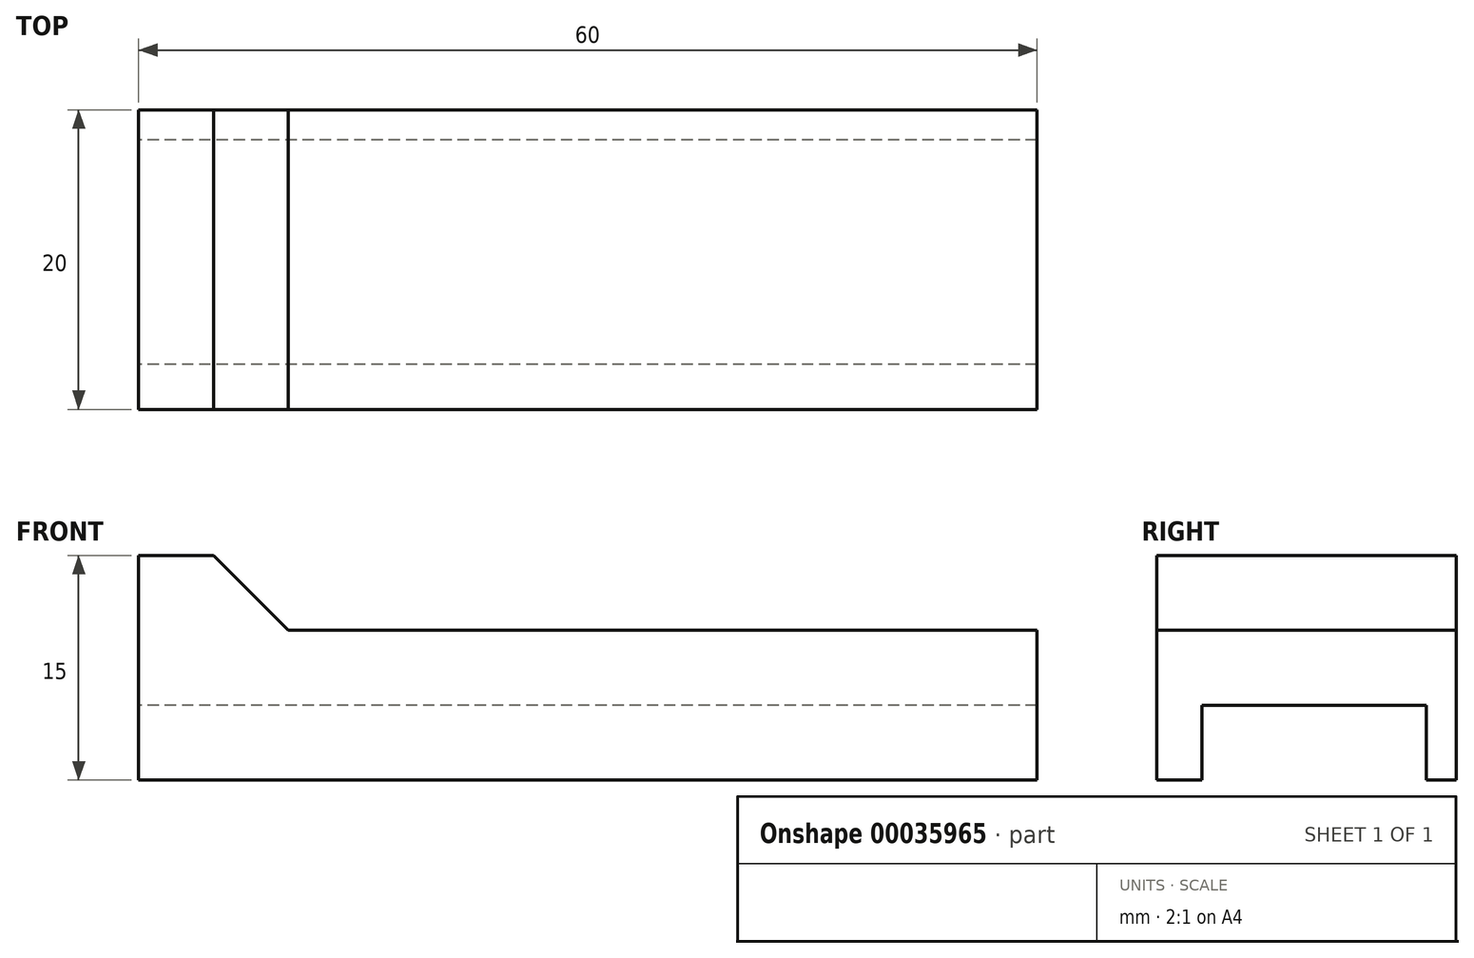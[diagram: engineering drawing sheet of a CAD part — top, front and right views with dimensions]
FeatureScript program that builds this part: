
annotation { "Feature Type Name" : "Feature", "Feature Type Description" : "" }
export const myFeature = defineFeature(function(context is Context, id is Id, definition is map)
    precondition{}
    {
        {
            var Q0;
            Q0=qCreatedBy(makeId("Right.planeOp"),FACE);
            var sketch = newSketch(context, id + "F0", { "sketchPlane" : qUnion([Q0])});
            skLineSegment(sketch, "E0", {"start": v(0, 0) * mm, "end": v(-2, 0) * mm});
            skLineSegment(sketch, "E1", {"start": v(-2, 0) * mm, "end": v(-2, 5) * mm});
            skLineSegment(sketch, "E2", {"start": v(-2, 5) * mm, "end": v(-17, 5) * mm});
            skLineSegment(sketch, "E3", {"start": v(-17, 5) * mm, "end": v(-17, 0) * mm});
            skLineSegment(sketch, "E4", {"start": v(-17, 0) * mm, "end": v(-20, 0) * mm});
            skLineSegment(sketch, "E5", {"start": v(-20, 0) * mm, "end": v(-20, 15) * mm});
            skLineSegment(sketch, "E6", {"start": v(-20, 15) * mm, "end": v(0, 15) * mm});
            skLineSegment(sketch, "E7", {"start": v(0, 15) * mm, "end": v(0, 0) * mm});
            skSolve(sketch);
        }
        {
            var Q0;
            Q0=makeQuery(id+"F0.imprint","IMPRINT",FACE,{"disambiguationData":[TD([[makeQuery(id+"F0.imprint","IMPRINT",EDGE,{"derivedFrom":sQuery(id+"F0.wireOp",EDGE,"E0")}),-1.0]])]});
            extrude(context, id + "F1", {"entities" : qUnion([Q0]), "depth" : 60 * mm});
        }
        {
            var Q0;
            Q0=qCreatedBy(makeId("Front.planeOp"),FACE);
            var sketch = newSketch(context, id + "F2", { "sketchPlane" : qUnion([Q0])});
            skLineSegment(sketch, "E8", {"start": v(65.65, 10) * mm, "end": v(10, 10) * mm});
            skLineSegment(sketch, "E9", {"start": v(10, 10) * mm, "end": v(2.52, 17.48) * mm});
            skLineSegment(sketch, "E10", {"start": v(2.52, 17.48) * mm, "end": v(62.52, 17.48) * mm});
            skLineSegment(sketch, "E11", {"start": v(62.52, 17.48) * mm, "end": v(65.65, 10) * mm});
            skSolve(sketch);
        }
        {
            var Q0;
            Q0=makeQuery(id+"F2.imprint","IMPRINT",FACE,{"disambiguationData":[TD([[makeQuery(id+"F2.imprint","IMPRINT",EDGE,{"derivedFrom":sQuery(id+"F2.wireOp",EDGE,"E8")}),-1.0]])]});
            extrude(context, id + "F3", {"entities" : qUnion([Q0]), "operationType" : NewBodyOperationType.REMOVE, "oppositeDirection" : true, "depth" : 25 * mm, "hasSecondDirection" : true, "secondDirectionOppositeDirection" : false, "secondDirectionDepth" : 25 * mm});
        }
    });
